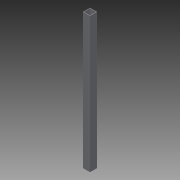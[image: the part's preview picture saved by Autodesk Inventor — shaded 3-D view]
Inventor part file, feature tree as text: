
AUTODESK INVENTOR PART (.ipt)
format: ipt  version: 2013 (Build 170138000, 138)  size: 71,168 bytes
history: native  units: in
note: dims shown in document units (in); Inventor stores cm internally (conversion verified against a paired STEP export)
features: extrude x1, sketch x1
ambient origin geometry x8: Origin, YZ Plane, XZ Plane, XY Plane, X Axis, Y Axis, Z Axis, Center Point
bodies: Solid1 (feature_tree)
feature tree (2):
  extrude  "Extrusion1"  Depth=1.0in
  sketch  "Sketch1"  dims[d0=1.0in d2=1.0in d3=0.875in d4=19.5in d5=0.0in]
